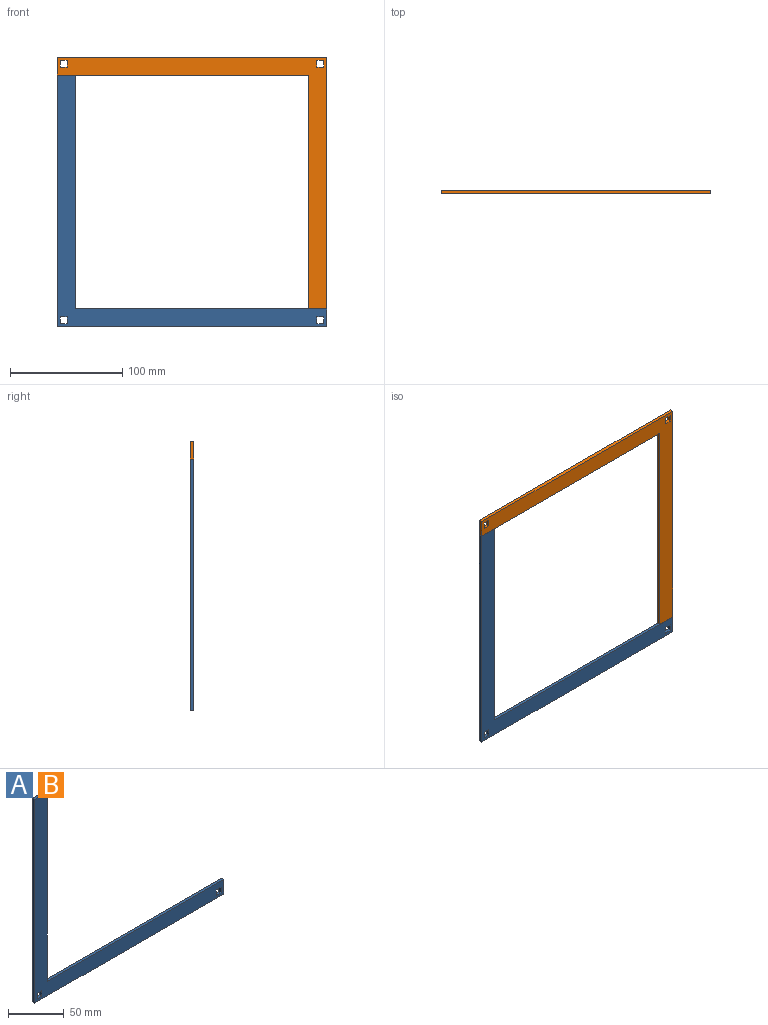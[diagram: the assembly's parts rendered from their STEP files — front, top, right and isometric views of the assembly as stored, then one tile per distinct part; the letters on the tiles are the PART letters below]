
ASSEMBLY  parts=2 mates=1
PART A: 16 faces, bbox 240x3x224 mm
  f0: plane 224x3mm, normal (-1,0,0), area 672mm2, adj f1,f5,f6,f15
  f1: plane 240x3mm, normal (0,0,-1), area 720mm2, adj f0,f4,f5,f6
  f2: plane 224x3mm, normal (0,0,1), area 672mm2, adj f3,f4,f5,f6
  f3: plane 208x3mm, normal (1,0,0), area 624mm2, adj f2,f5,f6,f15
  f4: plane 16x3mm, normal (1,0,0), area 48mm2, adj f1,f2,f5,f6
  f5: plane 240x224mm, normal (0,-1,0), area 7096mm2, adj f0,f1,f2,f3,f4,f7,f8,f9
  f6: plane 240x224mm, normal (0,1,0), area 7096mm2, adj f0,f1,f2,f3,f4,f7,f8,f9
  f7: plane 6x3mm, normal (-1,0,0), area 18mm2, adj f5,f6,f8,f10
  f8: plane 6x3mm, normal (0,0,1), area 18mm2, adj f5,f6,f7,f9
  f9: plane 6x3mm, normal (1,0,0), area 18mm2, adj f5,f6,f8,f10
  f10: plane 6x3mm, normal (0,0,-1), area 18mm2, adj f5,f6,f7,f9
  f11: plane 6x3mm, normal (0,0,-1), area 18mm2, adj f5,f6,f12,f14
  f12: plane 6x3mm, normal (-1,0,0), area 18mm2, adj f5,f6,f11,f13
  f13: plane 6x3mm, normal (0,0,1), area 18mm2, adj f5,f6,f12,f14
  f14: plane 6x3mm, normal (1,0,0), area 18mm2, adj f5,f6,f11,f13
  f15: plane 16x3mm, normal (0,0,1), area 48mm2, adj f0,f3,f5,f6
PART B: same geometry as A
PLACE A t=(-67.25,83.23,-35.58)mm
PLACE B rot(axis=(0,1,0),180deg) t=(172.75,83.23,204.42)mm
MATE fastened B.f15 <-> A.f2  axis (0,0,-1) through (172.75,83.23,-19.58)mm
